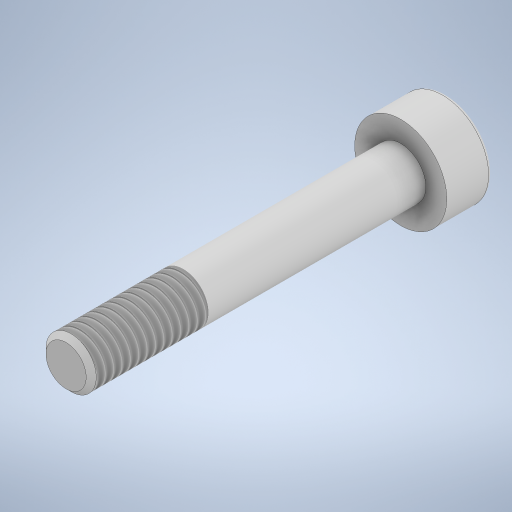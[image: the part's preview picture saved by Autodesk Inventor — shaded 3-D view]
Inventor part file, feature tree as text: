
AUTODESK INVENTOR PART (.ipt)
format: ipt  version: 2024 (Build 280153000, 153)  size: 307,712 bytes
history: native  units: in
note: dims shown in document units (in); Inventor stores cm internally (conversion verified against a paired STEP export)
features: extrude x3, sketch x2, plane x1, chamfer x1, thread x1, fillet x1, direct_edit x1, other x1
ambient origin geometry x8: Origin, YZ Plane, XZ Plane, XY Plane, X Axis, Y Axis, Z Axis, Center Point
bodies: Solid1 (feature_tree)
feature tree (11):
  sketch  "Sketch1"  dims[d0=0.2165in d1=0.1137in]
  extrude  "Extrusion1"  Depth=0.1137in
  extrude  "Extrusion2"  Depth=0.3937in TaperAngle=0.0deg
  plane  "Work Plane1"
  extrude  "Extrusion3"  TaperAngle=0.0deg  [1 undecoded]
  chamfer  "Chamfer1"  Distance=0.1181in
  thread  "Thread1"  [1 undecoded]
  fillet  "Fillet1"  Radius=0.0787in
  direct_edit  "Direct Edit1"
  sketch  "Sketch2"  dims[d2=0.1063in d3=0.0in d4=0.0492in d5=0.0in d6=0.0in d7=0.1181in d8=0.7874in d9=0.0in d10=0.0118in d11=0.0787in d12=45.0deg d13=0.7087in d14=0.0in d15=0.0079in d16=3.937in d17=0.3937in d18=0.3937in]
  other  "Scale1"
note: 2 required parameter values undecoded (feature->parameter linkage not recoverable at this tier; creation-order binding heuristic only, values carry confidence <= 0.55)
